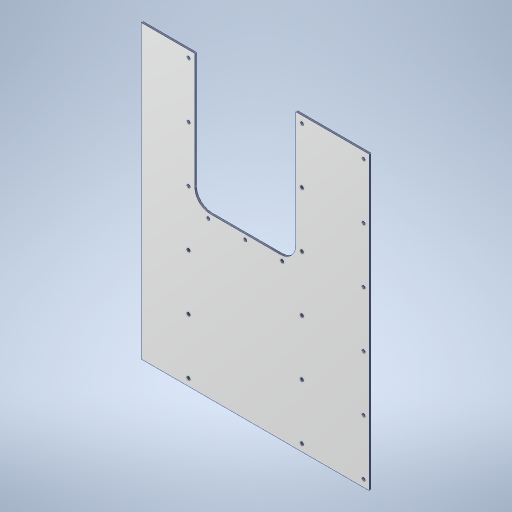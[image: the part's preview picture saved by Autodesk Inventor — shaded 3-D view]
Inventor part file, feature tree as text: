
AUTODESK INVENTOR PART (.ipt)
format: ipt  version: 2024 (Build 280153000, 153)  size: 359,424 bytes
history: native  units: mm
features: other x5, sketch x5, extrude x4, hole x2, reference x1
ambient origin geometry x8: Origin, YZ Plane, XZ Plane, XY Plane, X Axis, Y Axis, Z Axis, Center Point
bodies: Body1 (feature_tree), Body2 (feature_tree)
feature tree (17):
  other  "Laminate"
  sketch  "Sketch1"  dims[d0=370.0mm d1=473.0mm]
  extrude  "Extrusion1"  Depth=473.0mm
  extrude  "Extrusion2"  Depth=2.9mm TaperAngle=0.0deg
  extrude  "Extrusion3"  Depth=2.9mm
  hole  "Hole4"  [1 undecoded]
  sketch  "Sketch Driven Pattern1"  dims[d2=3.0mm d3=0.0mm d4=2.9mm d5=0.0mm]
  sketch  "Sketch9"  dims[d57=5.3mm d58=10.0mm d59=4.0mm d60=2.0mm d61=90.0deg d62=8.0mm d63=20.594885mm d71=450.0mm d73=100.0mm d74=184.0mm d75=60.0mm d77=90.0mm d78=10.0mm d80=10.0mm d82=10.0mm d83=10.0mm d84=1.0mm d85=214.0mm d86=120.0mm d87=8.0mm d88=5.3mm d89=6.0mm d90=4.0mm d91=2.0mm d92=90.0deg d93=8.0mm d94=20.594885mm d98=25.0mm d99=0.0mm d100=0.0mm]
  hole  "Hole5"  [1 undecoded]
  extrude  "Extrusion6"  Depth=25.0mm
  other  "Core"
  sketch  "Sketch6"  dims[d6=2.9mm d7=0.0mm d49=352.0mm]
  sketch  "Sketch8"  dims[d50=60.0mm d52=90.0mm d53=10.0mm d55=10.0mm]
  reference  "Reference1"
  parser-record x1  (decoder bookkeeping rows leaked as tree rows — omitted from the tree; the rows remain in map.json)
  other  "Left Internal Side Panel Assembly.iam"
  other  "Low Profile M5x8:13"
note: 2 required parameter values undecoded (feature->parameter linkage not recoverable at this tier; creation-order binding heuristic only, values carry confidence <= 0.55)
note: 1 file-system path scrubbed to <path> (originals preserved in map.json)
